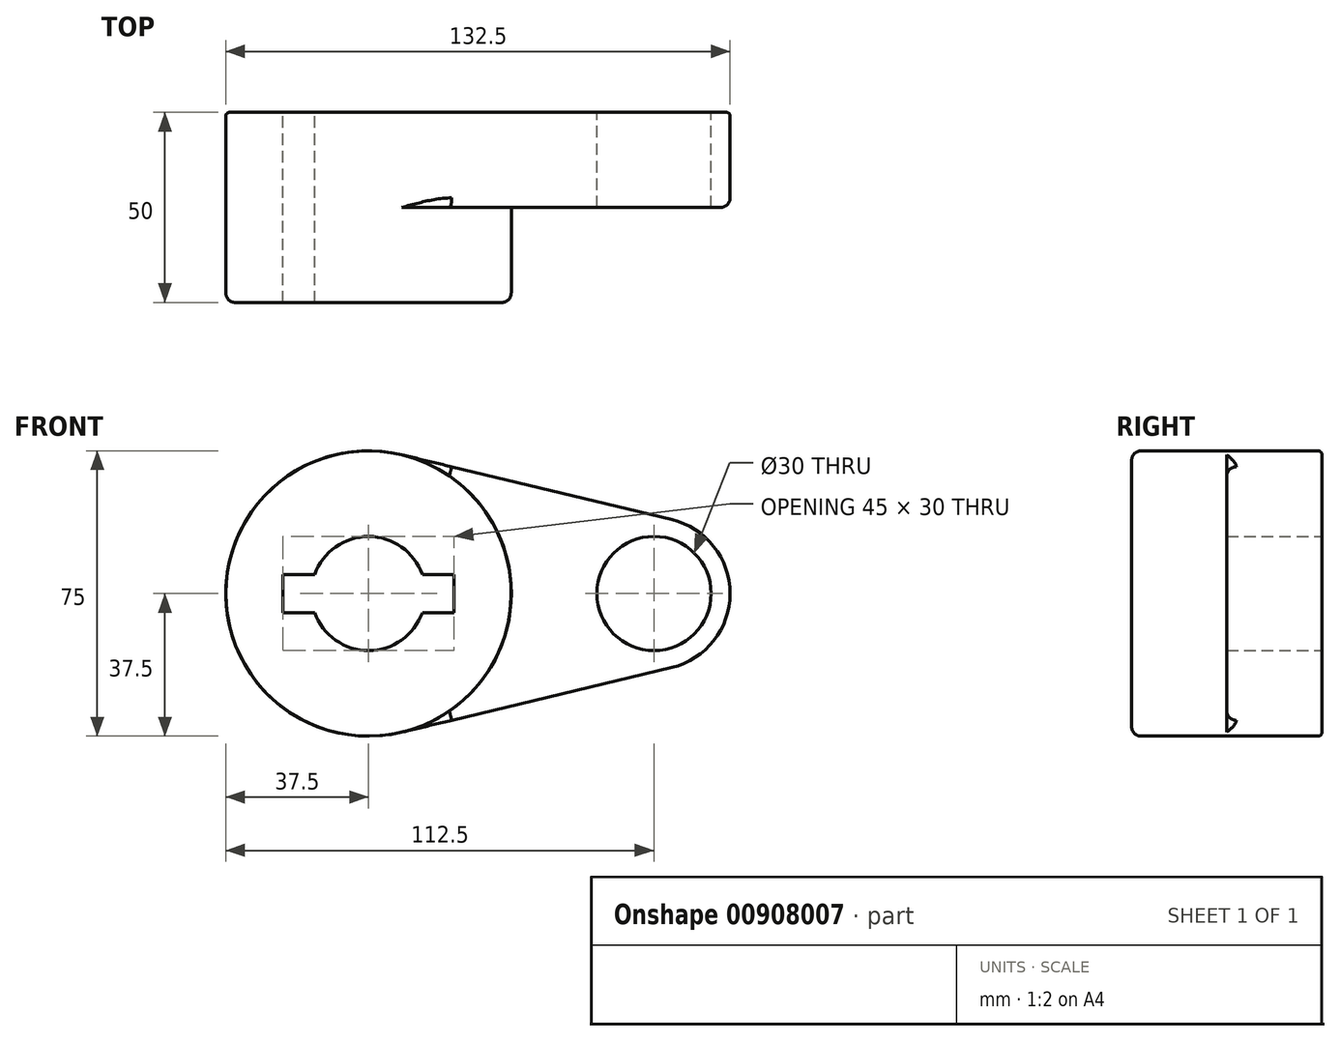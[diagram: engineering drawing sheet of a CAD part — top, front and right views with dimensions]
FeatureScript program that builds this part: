
annotation { "Feature Type Name" : "Feature", "Feature Type Description" : "" }
export const myFeature = defineFeature(function(context is Context, id is Id, definition is map)
    precondition{}
    {
        {
            var Q0;
            Q0=qCreatedBy(makeId("Front.planeOp"),FACE);
            var sketch = newSketch(context, id + "F0", { "sketchPlane" : qUnion([Q0])});
            skCircle(sketch, "E0", {"center": v(0, 0) * mm, "radius": 37.5 * mm});
            skCircle(sketch, "E1", {"center": v(75, 0) * mm, "radius": 20 * mm});
            skLineSegment(sketch, "E2", {"start": v(8.75, 36.46) * mm, "end": v(79.67, 19.45) * mm});
            skLineSegment(sketch, "E3", {"start": v(79.67, -19.45) * mm, "end": v(8.75, -36.46) * mm});
            skCircle(sketch, "E4", {"center": v(0, 0) * mm, "radius": 15 * mm});
            skCircle(sketch, "E5", {"center": v(75, 0) * mm, "radius": 15 * mm});
            skLineSegment(sketch, "E6.bottom", {"start": v(22.5, -5) * mm, "end": v(-22.5, -5) * mm});
            skLineSegment(sketch, "E6.top", {"start": v(22.5, 5) * mm, "end": v(-22.5, 5) * mm});
            skLineSegment(sketch, "E6.left", {"start": v(22.5, -5) * mm, "end": v(22.5, 5) * mm});
            skLineSegment(sketch, "E6.right", {"start": v(-22.5, -5) * mm, "end": v(-22.5, 5) * mm});
            skSolve(sketch);
        }
        {
            var Q0;
            {var subQ0=sQuery(id+"F0.wireOp",EDGE,"E2");Q0=makeQuery(id+"F0.imprint","IMPRINT",FACE,{"disambiguationData":[TD([[makeQuery(id+"F0.imprint","IMPRINT",EDGE,{"derivedFrom":subQ0}),-1.0]])]});}
            var Q1;
            Q1=makeQuery(id+"F0.imprint","IMPRINT",FACE,{"disambiguationData":[TD([[makeQuery(id+"F0.imprint","IMPRINT",EDGE,{"derivedFrom":sQuery(id+"F0.wireOp",EDGE,"E5")}),-1.0]])]});
            var Q2;
            {var subQ7=sQuery(id+"F0.wireOp",EDGE,"E6.left");Q2=makeQuery(id+"F0.imprint","IMPRINT",FACE,{"disambiguationData":[TD([[makeQuery(id+"F0.imprint","IMPRINT",EDGE,{"derivedFrom":subQ7}),-1.0]])]});}
            extrude(context, id + "F1", {"entities" : qUnion([Q0, Q1, Q2]), "depth" : 25 * mm, "offsetDistance" : 25 * mm});
        }
        {
            var Q0;
            Q0 = qSketchRegion(id + "FbKpOhEsRZU4tHD_0", true);
            var Q1;
            {var subQ7=sQuery(id+"F0.wireOp",EDGE,"E6.left");Q1=makeQuery(id+"F0.imprint","IMPRINT",FACE,{"disambiguationData":[TD([[makeQuery(id+"F0.imprint","IMPRINT",EDGE,{"derivedFrom":subQ7}),-1.0]])]});}
            extrude(context, id + "F2", {"entities" : qUnion([Q0, Q1]), "operationType" : NewBodyOperationType.ADD, "depth" : 50 * mm, "offsetDistance" : 25 * mm});
        }
        {
            var Q0;
            Q0=makeQuery(id+"F2.opExtrude","CAP_EDGE",EDGE,{"disambiguationData":[OSD([sQuery(id+"F0.wireOp",EDGE,"E0")])],"isStart":false});
            var Q1;
            Q1=makeQuery(id+"F1.opExtrude","CAP_EDGE",EDGE,{"disambiguationData":[OSD([sQuery(id+"F0.wireOp",EDGE,"E2")])],"isStart":false});
            var Q2;
            Q2=makeQuery(id+"F1.opExtrude","CAP_EDGE",EDGE,{"disambiguationData":[OSD([sQuery(id+"F0.wireOp",EDGE,"E1")])],"isStart":false});
            var Q3;
            Q3=makeQuery(id+"F1.opExtrude","CAP_EDGE",EDGE,{"disambiguationData":[OSD([sQuery(id+"F0.wireOp",EDGE,"E3")])],"isStart":false});
            fillet(context, id + "F3", {"entities" : qUnion([Q0, Q1, Q2, Q3]), "radius" : 2.5 * mm, "tangentPropagation" : true, "allowEdgeOverflow" : false});
        }
        {
            var Q0;
            Q0=makeQuery(id+"F1.opExtrude","CAP_EDGE",EDGE,{"disambiguationData":[OSD([sQuery(id+"F0.wireOp",EDGE,"E0")])],"isStart":true});
            var Q1;
            Q1=makeQuery(id+"F1.opExtrude","CAP_EDGE",EDGE,{"disambiguationData":[OSD([sQuery(id+"F0.wireOp",EDGE,"E2")])],"isStart":true});
            var Q2;
            Q2=makeQuery(id+"F1.opExtrude","CAP_EDGE",EDGE,{"disambiguationData":[OSD([sQuery(id+"F0.wireOp",EDGE,"E1")])],"isStart":true});
            var Q3;
            Q3=makeQuery(id+"F1.opExtrude","CAP_EDGE",EDGE,{"disambiguationData":[OSD([sQuery(id+"F0.wireOp",EDGE,"E3")])],"isStart":true});
            fillet(context, id + "F4", {"entities" : qUnion([Q0, Q1, Q2, Q3]), "radius" : 1 * mm, "tangentPropagation" : true, "allowEdgeOverflow" : false});
        }
    });
